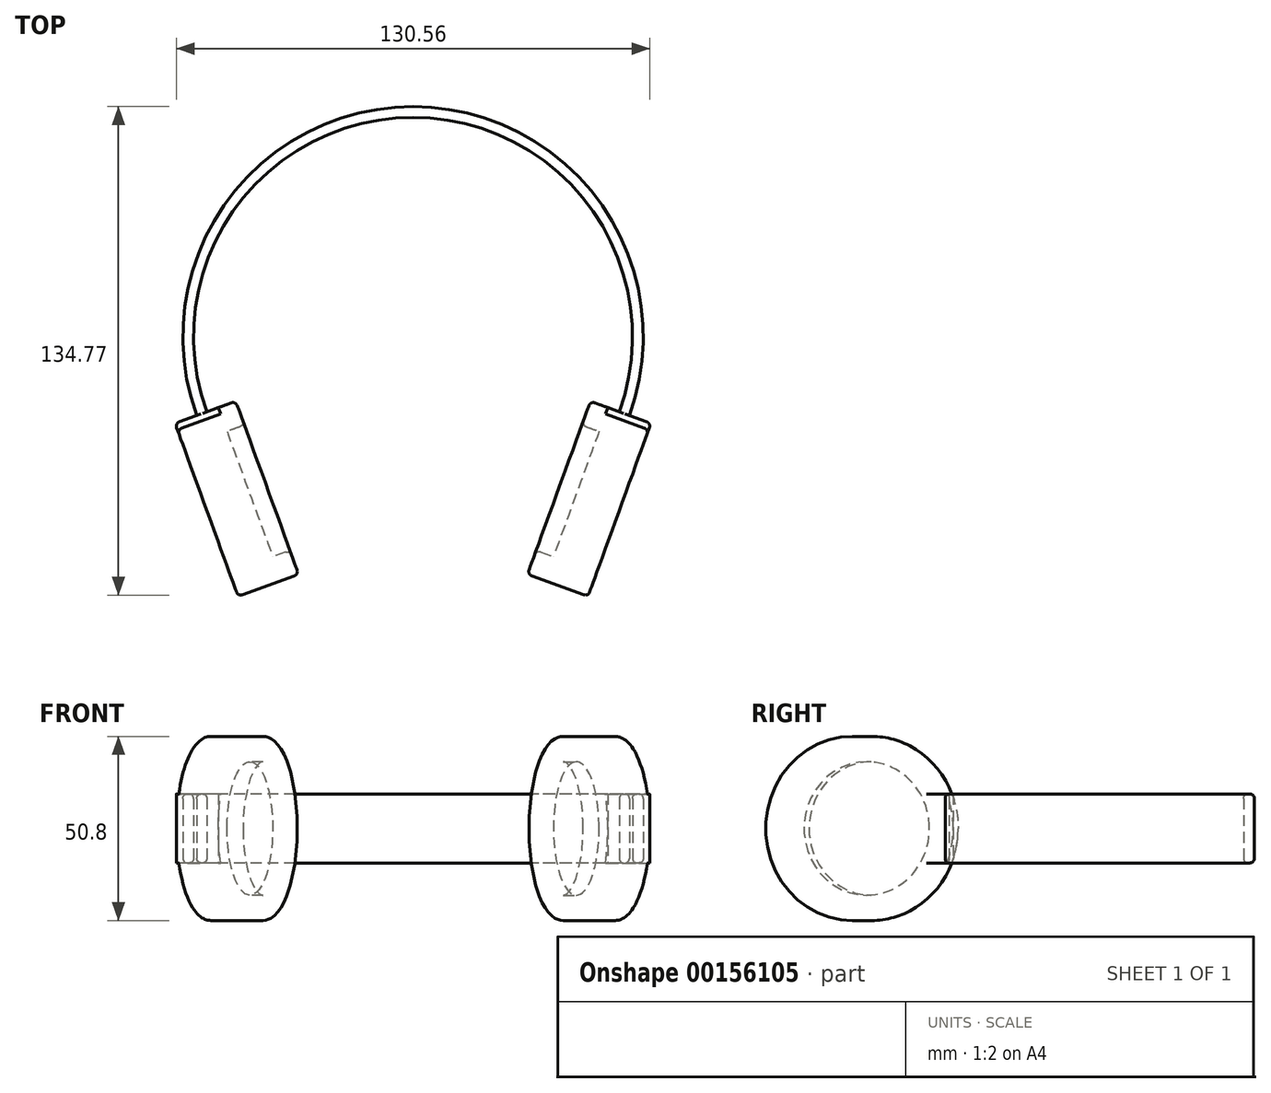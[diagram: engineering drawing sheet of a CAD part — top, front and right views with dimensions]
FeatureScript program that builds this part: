
annotation { "Feature Type Name" : "Feature", "Feature Type Description" : "" }
export const myFeature = defineFeature(function(context is Context, id is Id, definition is map)
    precondition{}
    {
        {
            var Q0;
            Q0=qCreatedBy(makeId("Top.planeOp"),FACE);
            var sketch = newSketch(context, id + "F0", { "sketchPlane" : qUnion([Q0])});
            skCircle(sketch, "E0", {"center": v(0, 0) * mm, "radius": 63.5 * mm});
            skCircle(sketch, "E1", {"center": v(0, 0) * mm, "radius": 60.53 * mm});
            skLineSegment(sketch, "E2", {"start": v(-59.67, -21.72) * mm, "end": v(0, 0) * mm, "construction": true});
            skLineSegment(sketch, "E3", {"start": v(0, 0) * mm, "end": v(59.67, -21.72) * mm, "construction": true});
            skLineSegment(sketch, "E4", {"start": v(-59.67, -21.72) * mm, "end": v(-56.88, -20.7) * mm});
            skLineSegment(sketch, "E5", {"start": v(59.67, -21.72) * mm, "end": v(56.88, -20.7) * mm});
            skSolve(sketch);
        }
        {
            var Q0;
            {var subQ0=sQuery(id+"F0.wireOp",EDGE,"E4");Q0=makeQuery(id+"F0.imprint","IMPRINT",FACE,{"disambiguationData":[TD([[makeQuery(id+"F0.imprint","IMPRINT",EDGE,{"derivedFrom":subQ0}),1.0]])]});}
            extrude(context, id + "F1", {"entities" : qUnion([Q0]), "endBound" : BoundingType.SYMMETRIC, "depth" : 19.05 * mm});
        }
        {
            var Q0;
            Q0=makeQuery(id+"F1.opExtrude","SWEPT_EDGE",EDGE,{"disambiguationData":[OSD([sQuery(id+"F0.wireOp",EDGE,"E0"),sQuery(id+"F0.wireOp",EDGE,"E4")])]});
            cPlane(context, id + "F2", {"entities" : qUnion([Q0]), "cplaneType" : CPlaneType.LINE_ANGLE, "offset" : 25.4 * mm, "angle" : 340 * degree, "width" : 152.4 * mm, "height" : 152.4 * mm});
        }
        {
            var Q0;
            Q0=qCreatedBy(id+"F2.planeOp",FACE);
            var sketch = newSketch(context, id + "F3", { "sketchPlane" : qUnion([Q0])});
            skLineSegment(sketch, "E6.0", {"start": v(0, 9.53) * mm, "end": v(0, -9.52) * mm});
            skLineSegment(sketch, "E7", {"start": v(0, 0) * mm, "end": v(50.8, 0) * mm, "construction": true});
            skArc(sketch, "E8", {"start": v(1.85, -9.52) * mm, "mid": v(50.8, 0) * mm, "end": v(1.85, 9.52) * mm});
            skLineSegment(sketch, "E9", {"start": v(0, -9.52) * mm, "end": v(1.85, -9.52) * mm});
            skLineSegment(sketch, "E10", {"start": v(0, 9.53) * mm, "end": v(1.85, 9.53) * mm});
            skSolve(sketch);
        }
        {
            var Q0;
            Q0 = qSketchRegion(id + "F3", true);
            extrude(context, id + "F4", {"entities" : qUnion([Q0]), "operationType" : NewBodyOperationType.ADD, "endBound" : BoundingType.SYMMETRIC, "oppositeDirection" : true, "depth" : 12.7 * mm});
        }
        {
            var Q0;
            Q0=makeQuery(id+"F4.opExtrude","CAP_FACE",FACE,{"disambiguationData":[OSD([sQuery(id+"F3.wireOp",EDGE,"E6.0"),sQuery(id+"F3.wireOp",EDGE,"E8"),sQuery(id+"F3.wireOp",EDGE,"E9"),sQuery(id+"F3.wireOp",EDGE,"E10")])],"isStart":false});
            var sketch = newSketch(context, id + "F5", { "sketchPlane" : qUnion([Q0])});
            skArc(sketch, "E11.0", {"start": v(-1.85, -9.52) * mm, "mid": v(-50.8, 0) * mm, "end": v(-1.85, 9.53) * mm});
            skCircle(sketch, "E12", {"center": v(-25.4, 0) * mm, "radius": 25.4 * mm});
            skCircle(sketch, "E13", {"center": v(-25.4, 0) * mm, "radius": 18.4 * mm});
            skSolve(sketch);
        }
        {
            var Q0;
            Q0 = qSketchRegion(id + "F5", true);
            extrude(context, id + "F6", {"entities" : qUnion([Q0]), "operationType" : NewBodyOperationType.ADD, "depth" : 5.08 * mm});
        }
        {
            var Q0;
            Q0=makeQuery(id+"F6.opExtrude","CAP_EDGE",EDGE,{"disambiguationData":[OSD([sQuery(id+"F5.wireOp",EDGE,"E13")])],"isStart":false});
            var Q1;
            Q1=makeQuery(id+"F6.opExtrude","CAP_EDGE",EDGE,{"disambiguationData":[OSD([sQuery(id+"F5.wireOp",EDGE,"E12")])],"isStart":false});
            var Q2;
            Q2=makeQuery(id+"F4.opExtrude","CAP_EDGE",EDGE,{"disambiguationData":[OSD([sQuery(id+"F3.wireOp",EDGE,"E8")])],"isStart":true});
            var Q3;
            Q3=makeQuery(id+"F4.opExtrude","CAP_EDGE",EDGE,{"disambiguationData":[OSD([sQuery(id+"F3.wireOp",EDGE,"E6.0")])],"isStart":true});
            var Q4;
            Q4=makeQuery(id+"F1.opExtrude","CAP_EDGE",EDGE,{"disambiguationData":[OSD([sQuery(id+"F0.wireOp",EDGE,"E0")])],"isStart":true});
            var Q5;
            Q5=makeQuery(id+"F1.opExtrude","CAP_EDGE",EDGE,{"disambiguationData":[OSD([sQuery(id+"F0.wireOp",EDGE,"E1")])],"isStart":true});
            var Q6;
            Q6=makeQuery(id+"F1.opExtrude","CAP_EDGE",EDGE,{"disambiguationData":[OSD([sQuery(id+"F0.wireOp",EDGE,"E0")])],"isStart":false});
            var Q7;
            Q7=makeQuery(id+"F1.opExtrude","CAP_EDGE",EDGE,{"disambiguationData":[OSD([sQuery(id+"F0.wireOp",EDGE,"E1")])],"isStart":false});
            fillet(context, id + "F7", {"entities" : qUnion([Q0, Q1, Q2, Q3, Q4, Q5, Q6, Q7]), "radius" : 1.27 * mm, "tangentPropagation" : true, "allowEdgeOverflow" : false});
        }
        {
            var Q0;
            Q0=makeQuery(id+"F1.opExtrude","SWEPT_BODY",BODY,{"disambiguationData":[OSD([sQuery(id+"F0.wireOp",EDGE,"E0"),sQuery(id+"F0.wireOp",EDGE,"E1"),sQuery(id+"F0.wireOp",EDGE,"E4"),sQuery(id+"F0.wireOp",EDGE,"E5")])]});
            var Q1;
            Q1=qCreatedBy(makeId("Right.planeOp"),FACE);
            mirror(context, id + "F8", {"operationType" : NewBodyOperationType.ADD, "entities" : qUnion([Q0]), "mirrorPlane" : qUnion([Q1])});
        }
    });
